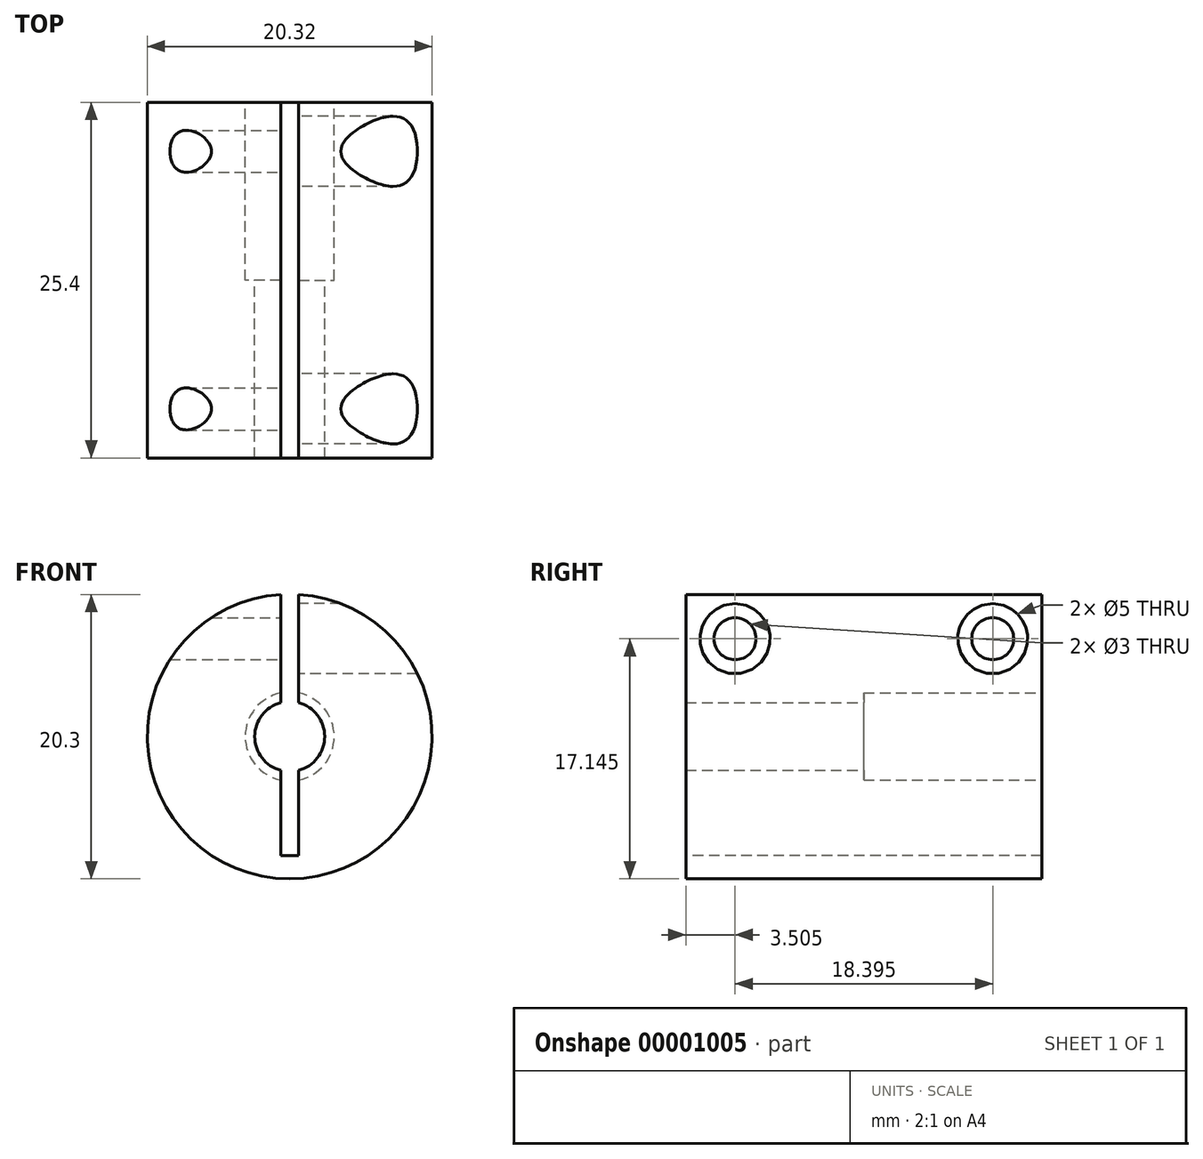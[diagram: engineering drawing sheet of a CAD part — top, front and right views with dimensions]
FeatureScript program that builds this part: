
annotation { "Feature Type Name" : "Feature", "Feature Type Description" : "" }
export const myFeature = defineFeature(function(context is Context, id is Id, definition is map)
    precondition{}
    {
        {
            var Q0;
            Q0=qCreatedBy(makeId("Front.planeOp"),FACE);
            var sketch = newSketch(context, id + "F0", { "sketchPlane" : qUnion([Q0])});
            skCircle(sketch, "E0", {"center": v(0, 0) * mm, "radius": 10.16 * mm});
            skCircle(sketch, "E1", {"center": v(0, 0) * mm, "radius": 3.18 * mm});
            skCircle(sketch, "E2", {"center": v(0, 0) * mm, "radius": 2.5 * mm});
            skSolve(sketch);
        }
        {
            var Q0;
            Q0=makeQuery(id+"F0.imprint","IMPRINT",FACE,{"disambiguationData":[TD([[makeQuery(id+"F0.imprint","IMPRINT",EDGE,{"derivedFrom":sQuery(id+"F0.wireOp",EDGE,"E0")}),1.0]])]});
            var Q1;
            Q1=makeQuery(id+"F0.imprint","IMPRINT",FACE,{"disambiguationData":[TD([[makeQuery(id+"F0.imprint","IMPRINT",EDGE,{"derivedFrom":sQuery(id+"F0.wireOp",EDGE,"E1")}),1.0]])]});
            extrude(context, id + "F1", {"entities" : qUnion([Q0, Q1]), "depth" : 25.4 * mm});
        }
        {
            var Q0;
            Q0=makeQuery(id+"F0.imprint","IMPRINT",FACE,{"disambiguationData":[TD([[makeQuery(id+"F0.imprint","IMPRINT",EDGE,{"derivedFrom":sQuery(id+"F0.wireOp",EDGE,"E1")}),1.0]])]});
            extrude(context, id + "F2", {"entities" : qUnion([Q0]), "operationType" : NewBodyOperationType.REMOVE, "depth" : 12.7 * mm});
        }
        {
            var Q0;
            Q0=qCreatedBy(makeId("Right.planeOp"),FACE);
            var sketch = newSketch(context, id + "F3", { "sketchPlane" : qUnion([Q0])});
            skCircle(sketch, "E3", {"center": v(-3.5, 6.98) * mm, "radius": 1.5 * mm});
            skCircle(sketch, "E4", {"center": v(-21.9, 6.98) * mm, "radius": 1.5 * mm});
            skSolve(sketch);
        }
        {
            var Q0;
            {Q0=qUnion([makeQuery(id+"F3.imprint","IMPRINT",FACE,{"disambiguationData":[TD([[makeQuery(id+"F3.imprint","IMPRINT",EDGE,{"derivedFrom":sQuery(id+"F3.wireOp",EDGE,"E3")}),1.0]])]}),makeQuery(id+"F3.imprint","IMPRINT",FACE,{"disambiguationData":[TD([[makeQuery(id+"F3.imprint","IMPRINT",EDGE,{"derivedFrom":sQuery(id+"F3.wireOp",EDGE,"E4")}),1.0]])]})]);}
            extrude(context, id + "F4", {"entities" : qUnion([Q0]), "operationType" : NewBodyOperationType.REMOVE, "endBound" : BoundingType.SYMMETRIC, "oppositeDirection" : true, "depth" : 25.4 * mm});
        }
        {
            var Q0;
            Q0=qCreatedBy(makeId("Right.planeOp"),FACE);
            var sketch = newSketch(context, id + "F5", { "sketchPlane" : qUnion([Q0])});
            skCircle(sketch, "E5", {"center": v(-21.9, 6.98) * mm, "radius": 2.5 * mm});
            skCircle(sketch, "E6", {"center": v(-3.5, 6.98) * mm, "radius": 2.5 * mm});
            skSolve(sketch);
        }
        {
            var Q0;
            Q0=makeQuery(id+"F5.imprint","IMPRINT",FACE,{"disambiguationData":[TD([[makeQuery(id+"F5.imprint","IMPRINT",EDGE,{"derivedFrom":sQuery(id+"F5.wireOp",EDGE,"E5")}),1.0]])]});
            var Q1;
            Q1=makeQuery(id+"F5.imprint","IMPRINT",FACE,{"disambiguationData":[TD([[makeQuery(id+"F5.imprint","IMPRINT",EDGE,{"derivedFrom":sQuery(id+"F5.wireOp",EDGE,"E6")}),1.0]])]});
            extrude(context, id + "F6", {"entities" : qUnion([Q0, Q1]), "operationType" : NewBodyOperationType.REMOVE, "depth" : 25.4 * mm});
        }
        {
            var Q0;
            Q0=makeQuery(id+"F1.opExtrude","CAP_FACE",FACE,{"disambiguationData":[OSD([sQuery(id+"F0.wireOp",EDGE,"E0"),sQuery(id+"F0.wireOp",EDGE,"E2")])],"isStart":false});
            var sketch = newSketch(context, id + "F7", { "sketchPlane" : qUnion([Q0])});
            skLineSegment(sketch, "E7.rect.bottom", {"start": v(-0.64, 11.63) * mm, "end": v(0.64, 11.63) * mm});
            skLineSegment(sketch, "E7.rect.left", {"start": v(-0.64, 11.63) * mm, "end": v(-0.64, -8.51) * mm});
            skLineSegment(sketch, "E7.rect.right", {"start": v(0.64, 11.63) * mm, "end": v(0.64, -8.51) * mm});
            skPoint(sketch, "E7.rect.middle", {"position": v(0, 0) * mm});
            skLineSegment(sketch, "E8", {"start": v(-0.64, -8.51) * mm, "end": v(0.64, -8.51) * mm});
            skPoint(sketch, "E9.orphan", {"position": v(-0.64, -11.63) * mm});
            skPoint(sketch, "E10.orphan", {"position": v(0.64, -11.63) * mm});
            skSolve(sketch);
        }
        {
            var Q0;
            {var subQ0=makeQuery(id+"F1.opExtrude","CAP_EDGE",EDGE,{"disambiguationData":[OSD([sQuery(id+"F0.wireOp",EDGE,"E0")])],"isStart":false});var subQ3=sQuery(id+"F7.wireOp",EDGE,"E7.rect.left");var subQ4=makeQuery(id+"F7.imprint","INTERSECT",VERTEX,{"derivedFrom":[subQ0,subQ3]});var subQ6=sQuery(id+"F7.wireOp",EDGE,"E7.rect.bottom");var subQ7=makeQuery(id+"F1.opExtrude","CAP_EDGE",EDGE,{"disambiguationData":[OSD([sQuery(id+"F0.wireOp",EDGE,"E2")])],"isStart":false});var subQ11=sQuery(id+"F7.wireOp",EDGE,"E8");var subQ13=makeQuery(id+"F7.imprint","INTERSECT",VERTEX,{"disambiguationData":[OD(0.0)],"derivedFrom":[subQ7,subQ3]});Q0=qUnion([makeQuery(id+"F7.imprint","IMPRINT",FACE,{"disambiguationData":[TD([[makeQuery(id+"F7.imprint","IMPRINT",EDGE,{"derivedFrom":subQ6}),-1.0]])]}),makeQuery(id+"F7.imprint","IMPRINT",FACE,{"disambiguationData":[TD([[makeQuery(id+"F7.imprint","IMPRINT",EDGE,{"derivedFrom":subQ11}),1.0]])]}),makeQuery(id+"F7.imprint","IMPRINT",FACE,{"disambiguationData":[TD([[makeQuery(id+"F7.imprint","IMPRINT",EDGE,{"disambiguationData":[TD([[subQ4,-1.0]])],"derivedFrom":subQ3}),1.0]])]}),makeQuery(id+"F7.imprint","IMPRINT",FACE,{"disambiguationData":[TD([[makeQuery(id+"F7.imprint","IMPRINT",EDGE,{"disambiguationData":[TD([[subQ13,-1.0]])],"derivedFrom":subQ3}),1.0]])]})]);}
            var Q1;
            Q1=sQuery(id+"F7.wireOp",EDGE,"1ef5ef41-197a-4857-9480-4588381af675.right");
            extrude(context, id + "F8", {"entities" : qUnion([Q0]), "operationType" : NewBodyOperationType.REMOVE, "surfaceEntities" : qUnion([Q1]), "endBound" : BoundingType.THROUGH_ALL, "oppositeDirection" : true, "depth" : 25.4 * mm});
        }
    });
